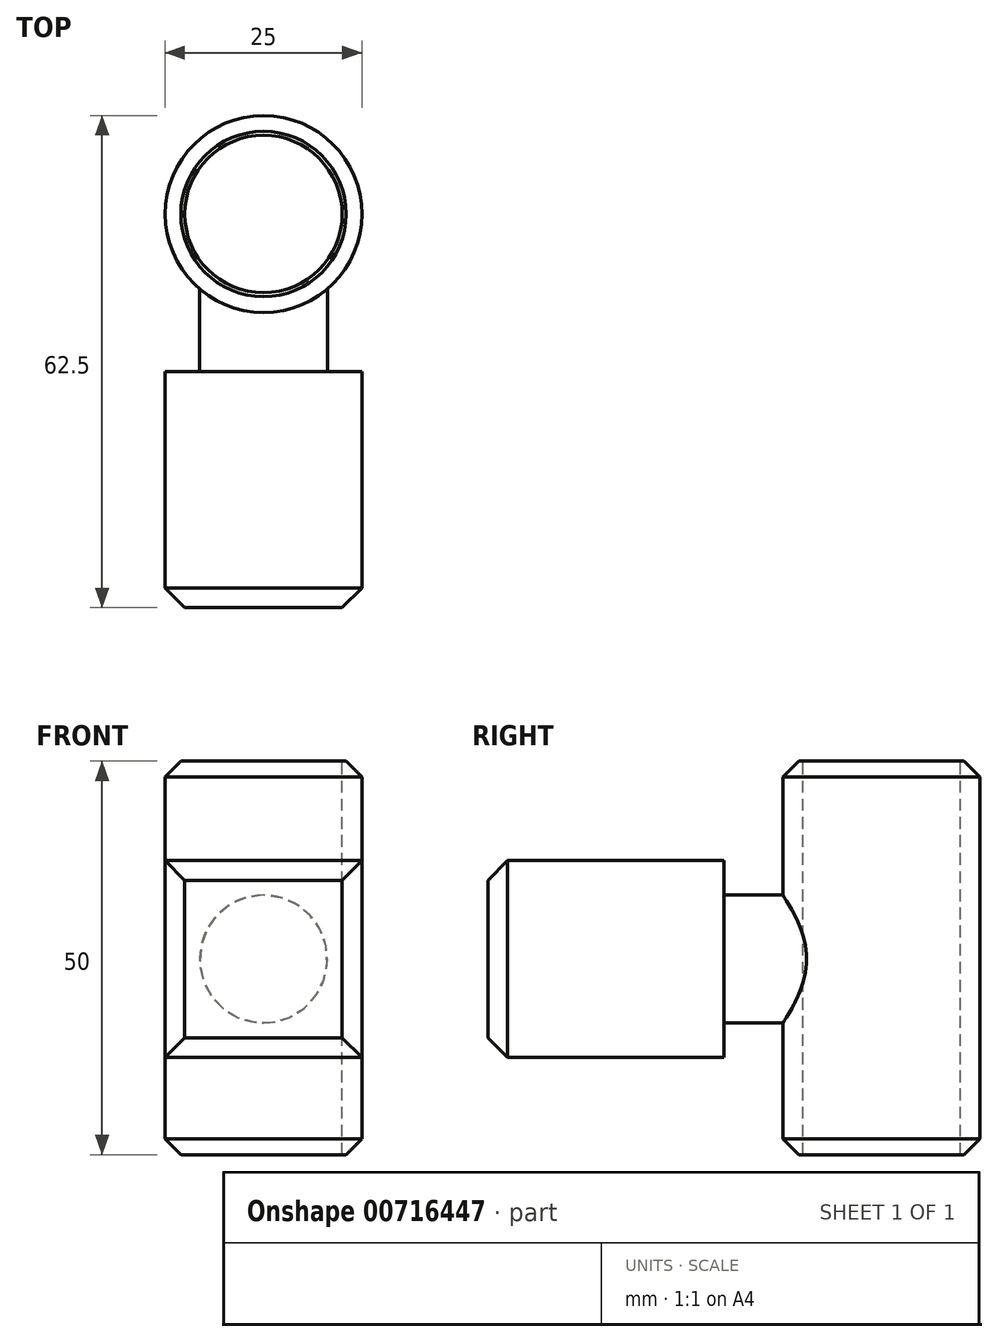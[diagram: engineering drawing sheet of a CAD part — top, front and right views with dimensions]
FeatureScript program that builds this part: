
annotation { "Feature Type Name" : "Feature", "Feature Type Description" : "" }
export const myFeature = defineFeature(function(context is Context, id is Id, definition is map)
    precondition{}
    {
        {
            var Q0;
            Q0=qCreatedBy(makeId("Top.planeOp"),FACE);
            var sketch = newSketch(context, id + "F0", { "sketchPlane" : qUnion([Q0])});
            skCircle(sketch, "E0", {"center": v(0, 0) * mm, "radius": 12.5 * mm});
            skSolve(sketch);
        }
        {
            var Q0;
            Q0 = qSketchRegion(id + "F0", true);
            extrude(context, id + "F1", {"entities" : qUnion([Q0]), "depth" : 50 * mm, "offsetDistance" : 25 * mm});
        }
        {
            var Q0;
            Q0=makeQuery(id+"F1.opExtrude","CAP_EDGE",EDGE,{"disambiguationData":[OSD([sQuery(id+"F0.wireOp",EDGE,"E0")])],"isStart":false});
            var Q1;
            Q1=makeQuery(id+"F1.opExtrude","CAP_EDGE",EDGE,{"disambiguationData":[OSD([sQuery(id+"F0.wireOp",EDGE,"E0")])],"isStart":true});
            chamfer(context, id + "F2", {"entities" : qUnion([Q0, Q1]), "width" : 2 * mm, "tangentPropagation" : true});
        }
        {
            var Q0;
            Q0=qCreatedBy(makeId("Front.planeOp"),FACE);
            var sketch = newSketch(context, id + "F3", { "sketchPlane" : qUnion([Q0])});
            skCircle(sketch, "E1", {"center": v(0, 24.86) * mm, "radius": 8.1 * mm});
            skSolve(sketch);
        }
        {
            var Q0;
            Q0 = qSketchRegion(id + "F3", true);
            extrude(context, id + "F4", {"entities" : qUnion([Q0]), "operationType" : NewBodyOperationType.ADD, "depth" : 20 * mm, "offsetDistance" : 25 * mm});
        }
        {
            var Q0;
            Q0=makeQuery(id+"F4.opExtrude","CAP_FACE",FACE,{"disambiguationData":[OSD([sQuery(id+"F3.wireOp",EDGE,"E1")])],"isStart":false});
            var sketch = newSketch(context, id + "F5", { "sketchPlane" : qUnion([Q0])});
            skLineSegment(sketch, "E2.bottom", {"start": v(-12.5, 37.36) * mm, "end": v(12.5, 37.36) * mm});
            skLineSegment(sketch, "E2.top", {"start": v(-12.5, 12.36) * mm, "end": v(12.5, 12.36) * mm});
            skLineSegment(sketch, "E2.left", {"start": v(-12.5, 37.36) * mm, "end": v(-12.5, 12.36) * mm});
            skLineSegment(sketch, "E2.right", {"start": v(12.5, 37.36) * mm, "end": v(12.5, 12.36) * mm});
            skPoint(sketch, "E2.middle", {"position": v(0, 24.86) * mm});
            skSolve(sketch);
        }
        {
            var Q0;
            Q0 = qSketchRegion(id + "F5", true);
            extrude(context, id + "F6", {"entities" : qUnion([Q0]), "operationType" : NewBodyOperationType.ADD, "depth" : 30 * mm, "offsetDistance" : 25 * mm});
        }
        {
            var Q0;
            Q0=makeQuery(id+"F6.opExtrude","CAP_FACE",FACE,{"disambiguationData":[OSD([sQuery(id+"F5.wireOp",EDGE,"E2.bottom"),sQuery(id+"F5.wireOp",EDGE,"E2.top"),sQuery(id+"F5.wireOp",EDGE,"E2.left"),sQuery(id+"F5.wireOp",EDGE,"E2.right")])],"isStart":false});
            chamfer(context, id + "F7", {"entities" : qUnion([Q0]), "width" : 2.5 * mm, "tangentPropagation" : true});
        }
        {
            var Q0;
            Q0=makeQuery(id+"F1.opExtrude","CAP_FACE",FACE,{"disambiguationData":[OSD([sQuery(id+"F0.wireOp",EDGE,"E0")])],"isStart":false});
            var sketch = newSketch(context, id + "F8", { "sketchPlane" : qUnion([Q0])});
            skCircle(sketch, "E3", {"center": v(0, 0) * mm, "radius": 10 * mm});
            skSolve(sketch);
        }
        {
            var Q0;
            Q0 = qSketchRegion(id + "F8", true);
            extrude(context, id + "F9", {"entities" : qUnion([Q0]), "operationType" : NewBodyOperationType.REMOVE, "endBound" : BoundingType.THROUGH_ALL, "oppositeDirection" : true, "depth" : 25 * mm, "offsetDistance" : 25 * mm});
        }
    });
